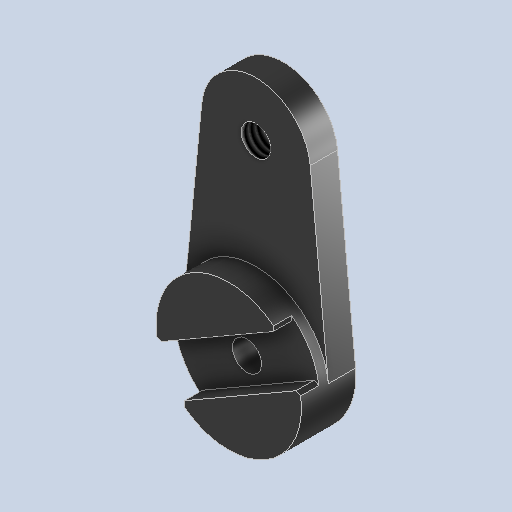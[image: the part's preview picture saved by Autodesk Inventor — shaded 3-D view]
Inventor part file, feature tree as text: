
AUTODESK INVENTOR PART (.ipt)
format: ipt  version: 2024.2 (Build 282272000, 272)  size: 286,208 bytes
history: native  units: mm
features: other x3, chamfer x1
ambient origin geometry x8: Origin, YZ Plane, XZ Plane, XY Plane, X Axis, Y Axis, Z Axis, Center Point
bodies: Solid1 (feature_tree)
feature tree (4):
  other  "LongCrankFrameBasis.ipt"
  chamfer  "C0.5"  Distance=10.0mm
  other  "Solid1::LongCrankFrameBasis.ipt"
  other  "TaggingFeature1"
